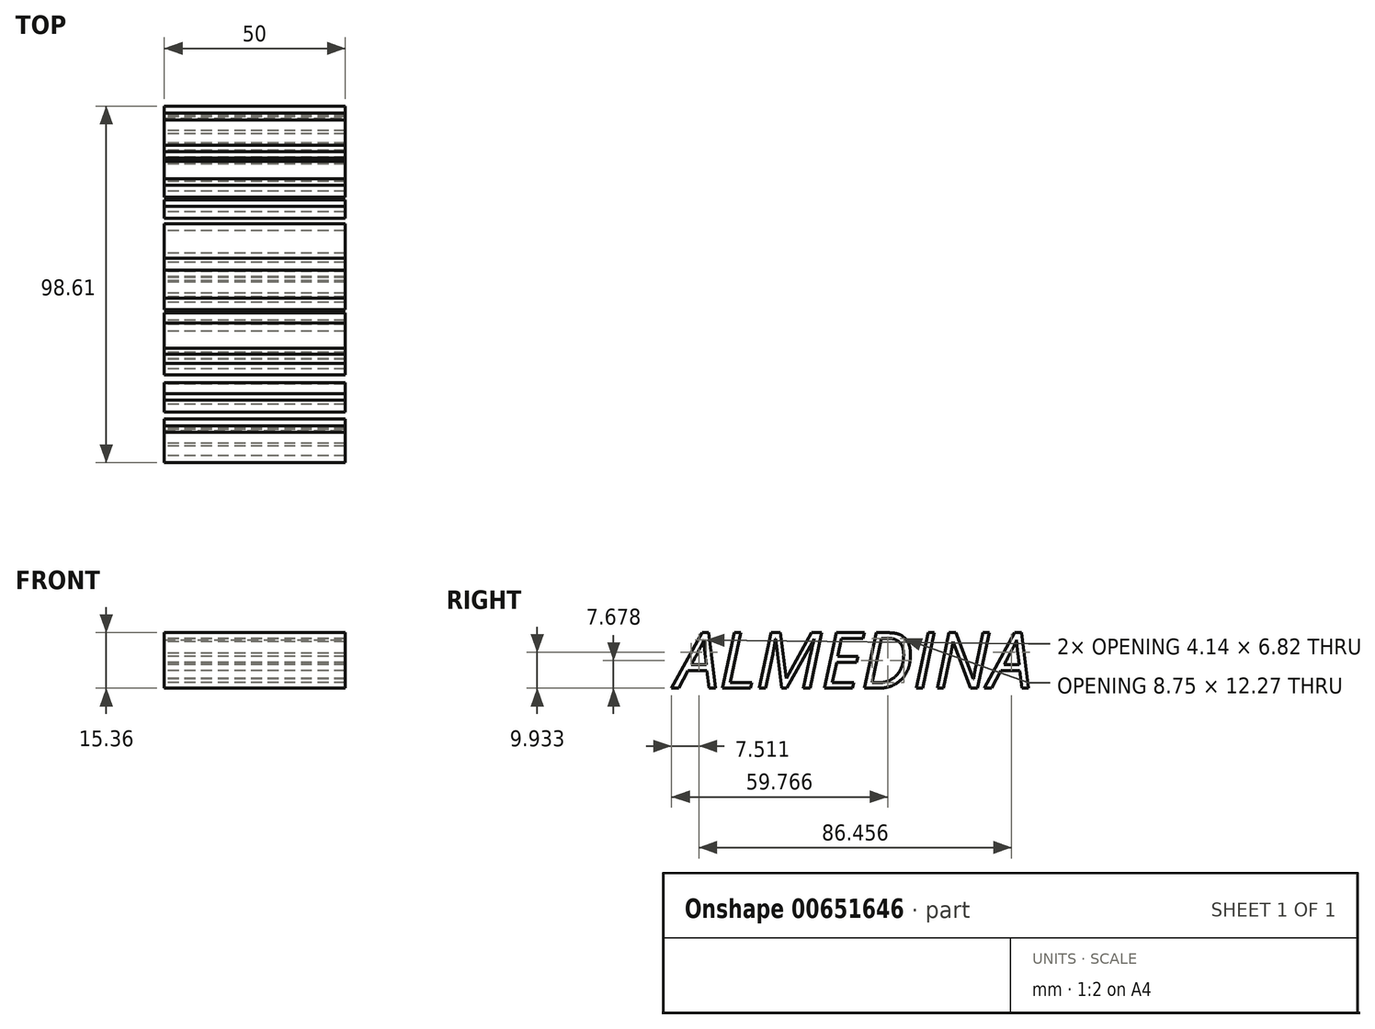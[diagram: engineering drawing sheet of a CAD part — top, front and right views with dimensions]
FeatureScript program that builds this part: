
annotation { "Feature Type Name" : "Feature", "Feature Type Description" : "" }
export const myFeature = defineFeature(function(context is Context, id is Id, definition is map)
    precondition{}
    {
        {
            var Q0;
            Q0=qCreatedBy(makeId("Right.planeOp"),FACE);
            var sketch = newSketch(context, id + "F0", { "sketchPlane" : qUnion([Q0])});
            skText(sketch, "E0", { "text": "ALMEDINA", "fontName": "OpenSans-Italic.ttf"});
            const initialGuessF0  = {"E0": [-0.03564, 0.0132, 1, 0, 0.01549]};
            skSetInitialGuess(sketch, initialGuessF0);
            skSolve(sketch);
        }
        {
            var Q0;
            Q0 = qSketchRegion(id + "F0", true);
            extrude(context, id + "F1", {"entities" : qUnion([Q0]), "endBound" : BoundingType.SYMMETRIC, "depth" : 50 * mm, "offsetDistance" : 25 * mm});
        }
    });
